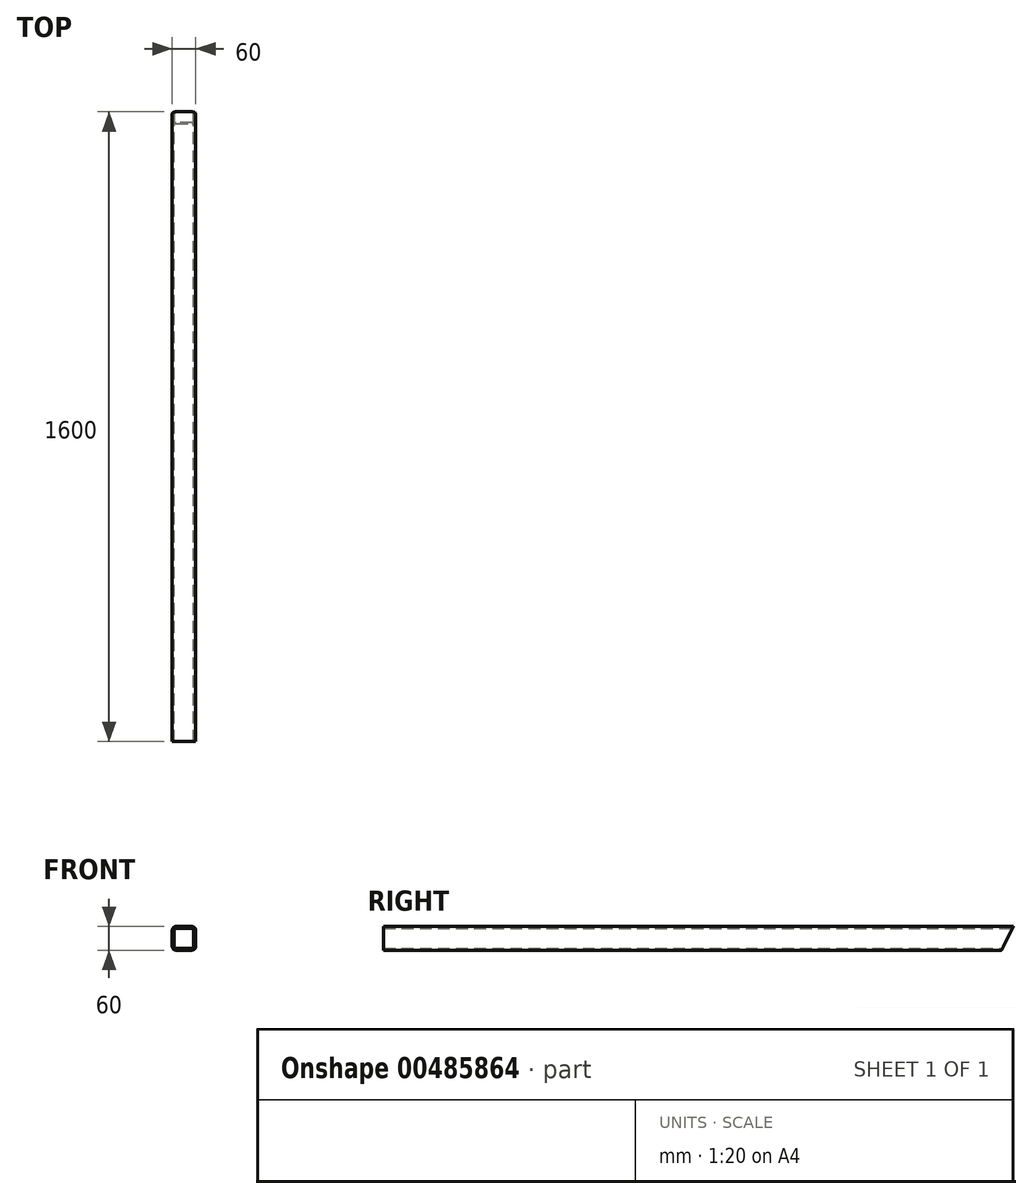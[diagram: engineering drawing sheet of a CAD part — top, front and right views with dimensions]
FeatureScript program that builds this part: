
annotation { "Feature Type Name" : "Feature", "Feature Type Description" : "" }
export const myFeature = defineFeature(function(context is Context, id is Id, definition is map)
    precondition{}
    {
        {
            var Q0;
            Q0=qCreatedBy(makeId("Front.planeOp"),FACE);
            var sketch = newSketch(context, id + "F0", { "sketchPlane" : qUnion([Q0])});
            skLineSegment(sketch, "E0.bottom", {"start": v(20, 30) * mm, "end": v(-20, 30) * mm});
            skLineSegment(sketch, "E0.top", {"start": v(20, -30) * mm, "end": v(-20, -30) * mm});
            skLineSegment(sketch, "E0.left", {"start": v(30, 20) * mm, "end": v(30, -20) * mm});
            skLineSegment(sketch, "E0.right", {"start": v(-30, 20) * mm, "end": v(-30, -20) * mm});
            skPoint(sketch, "E0.middle", {"position": v(0, 0) * mm});
            skPoint(sketch, "E1.visualSharp", {"position": v(-30, 30) * mm});
            skArc(sketch, "E1.filletArc", {"start": v(-20, 30) * mm, "mid": v(-27.07, 27.07) * mm, "end": v(-30, 20) * mm});
            skPoint(sketch, "E2.visualSharp", {"position": v(30, 30) * mm});
            skArc(sketch, "E2.filletArc", {"start": v(30, 20) * mm, "mid": v(27.07, 27.07) * mm, "end": v(20, 30) * mm});
            skPoint(sketch, "E3.visualSharp", {"position": v(30, -30) * mm});
            skArc(sketch, "E3.filletArc", {"start": v(20, -30) * mm, "mid": v(27.07, -27.07) * mm, "end": v(30, -20) * mm});
            skPoint(sketch, "E4.visualSharp", {"position": v(-30, -30) * mm});
            skArc(sketch, "E4.filletArc", {"start": v(-30, -20) * mm, "mid": v(-27.07, -27.07) * mm, "end": v(-20, -30) * mm});
            skArc(sketch, "E5.0", {"start": v(25, 20) * mm, "mid": v(23.54, 23.54) * mm, "end": v(20, 25) * mm});
            skLineSegment(sketch, "E5.1", {"start": v(25, 20) * mm, "end": v(25, -20) * mm});
            skLineSegment(sketch, "E5.2", {"start": v(20, 25) * mm, "end": v(-20, 25) * mm});
            skArc(sketch, "E5.3", {"start": v(20, -25) * mm, "mid": v(23.54, -23.54) * mm, "end": v(25, -20) * mm});
            skArc(sketch, "E5.4", {"start": v(-20, 25) * mm, "mid": v(-23.54, 23.54) * mm, "end": v(-25, 20) * mm});
            skLineSegment(sketch, "E5.5", {"start": v(-25, 20) * mm, "end": v(-25, -20) * mm});
            skArc(sketch, "E5.6", {"start": v(-25, -20) * mm, "mid": v(-23.54, -23.54) * mm, "end": v(-20, -25) * mm});
            skLineSegment(sketch, "E5.7", {"start": v(20, -25) * mm, "end": v(-20, -25) * mm});
            skSolve(sketch);
        }
        {
            var Q0;
            Q0 = qSketchRegion(id + "F0", true);
            extrude(context, id + "F1", {"entities" : qUnion([Q0]), "endBound" : BoundingType.SYMMETRIC, "depth" : 1600 * mm});
        }
        {
            var Q0;
            Q0=makeQuery(id+"F1.opExtrude","SWEPT_FACE",FACE,{"disambiguationData":[OSD([sQuery(id+"F0.wireOp",EDGE,"E0.left")])]});
            var sketch = newSketch(context, id + "F2", { "sketchPlane" : qUnion([Q0])});
            skLineSegment(sketch, "E6", {"start": v(800, 30) * mm, "end": v(770, -30) * mm});
            skLineSegment(sketch, "E7", {"start": v(770, -30) * mm, "end": v(800, -30) * mm});
            skLineSegment(sketch, "E8", {"start": v(800, -30) * mm, "end": v(800, 30) * mm});
            skSolve(sketch);
        }
        {
            var Q0;
            Q0 = qSketchRegion(id + "F2", true);
            extrude(context, id + "F3", {"entities" : qUnion([Q0]), "operationType" : NewBodyOperationType.REMOVE, "endBound" : BoundingType.THROUGH_ALL, "oppositeDirection" : true, "depth" : 25 * mm});
        }
    });
